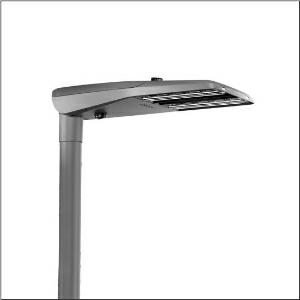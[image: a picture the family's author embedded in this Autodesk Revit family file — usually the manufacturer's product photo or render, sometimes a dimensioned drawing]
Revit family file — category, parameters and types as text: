
# Revit family: streetlight_sl_11_iq_midi___st1_2a_5xc3a51y08me_2b41
name_source: partatom
category: Lighting Fixtures
units: mm (PartAtom-declared; Revit-internal decimal feet)

## family parameters
Cut with Voids When Loaded = No
Host = Face
Light Source = No
Part Type = Normal
Room Calculation Point = No
Round Connector Dimension = Use Diameter
Shared = No

## types (1)
- --- (1 x LED, 18110 lm, 122.7 W, 3000K)
    Apparent Load = 123 VA
    CIE Flux Codes = 32 70 96 100 100
    Color Rendering = 70
    Color Temperature = 3000K
    Default Elevation = 1800 mm
    Description = Streetlight SL 11 iQ midi, mast luminaire, primary light control with 3 zone facetted reflector, of plastic, silver coated, highly specular, primary optical cover: cover, of PMMA, transparent, light distribution: ST1.2a, light emission: direct distribution, primary light characteristic: asymmetric, installation type: post-top, side-entry, lamps: LED, High Power LED, rated values: 18.110lm | 122,7W | 147,6lm/W (begin service life); end service life: 18.110lm | 130,2W; at 50% lumin. flux: 9.055lm | 56,1W | 161,4lm/W, colour temperature: 3000K, colour rendering: CRI > 70, light colour: 730, light setting 1 begin service life: 100% | 18.110lm | 122,7W | 147,6lm/W | 3.000K, light setting 1 end service life: 130,2W, further light settings possible, control: pre-setting: logarithmic dimming characteristic, Street-Remote, Auto-Match, Temp-Guard, Lumen-Switch, Night-Set, Smart-Wire, Light-Fading, Desk-Remote (wireless, voltage-free reading and setting of iQ features in the workshop via application-optimized NFC function/RFID function), optimised constant luminous flux control (CLO 2.0), with cable H07RN-F 3x 1.5mm², mains connection: 230..240V, AC, 50/60Hz, connection cable pre-assembled, cable length: 12,5m, luminaire housing, of diecast aluminium, powder-coated, SITECO metallic grey (DB 702S), please order mast flange separately, inclination adjustable without tools: 0°, 5°, 10°, 15° (post-top) | 0°, -5°, -10°, -15° (side-entry), sealing non-destructively replaceable, multi-level sealing system, length: 780mm, width: 376mm, height: 118mm, mast flange for spigot size: 42mm (side-entry): 5XC10008XM4, 60/48mm (side-entry/post-top): 5XC10108XM2, 76/60mm (side-entry/post-top): 5XC10108XM1, equipment: Power, Smart Interface below and above, protection rating (complete): IP66, insulation class (complete): insulation class II (safety insulation), certification: CE, ENEC, ENEC+, VDE, UKCA, impact resistance: IK10, permissible operating ambient temperature for outdoor applications: -25..+50°C, standard-compliant lighting for roads and squares, Environmental Product Declaration (EPD) tested and certified by an independent institute, packaging unit: 1 piece

Light Distribution: ST1.2a
    Height = 118 mm
    Lamp = 1 x LED
    Lamp Light Flux = 18110 lm
    Lamp Power = 122.7 W
    Lamp count = 1
    Length = 780 mm
    Luminous efficacy = 148 lm/W
    Manufacturer = Siteco
    ModVariant = No
    Model = 5XC3A51Y08ME
    Number of Poles = 1
    OnlyDefault = Yes
    Power Factor = 1
    Product Name = Streetlight SL 11 iQ midi | ST1.2a
    Product group = mast luminaire | pylon top
    ProductGroupID = 6100
    Protection Class = Protection class II
    Protection Degree = IP 66
    RLX_Detail_Level = 1
    RLX_Emergency_Light_Flux = 0 lm
    RLX_Emergency_Type = 0
    RLX_Emergency_Type_DB = No
    RlxData = <blob elided: 70157 chars, md5=62decb13>
    Socket = socket
    Standby Power = 0 W
    System Light Flux = 18111 lm
    System Power = 123 W
    Type Comments = factory setting: luminous flux: 100 % | dim-lin: 254 | 553 mA
    Type Image = l_1004429.jpg
    URL = http://relux.com
    VarID = @adj_132803
    Voltage = 0 V
    Weight = 0.00 kg
    Width = 376 mm

## geometry (parser evidence)
native form markers: Blend x4, Sweep x10
no freeform markers — native parametric forms only
